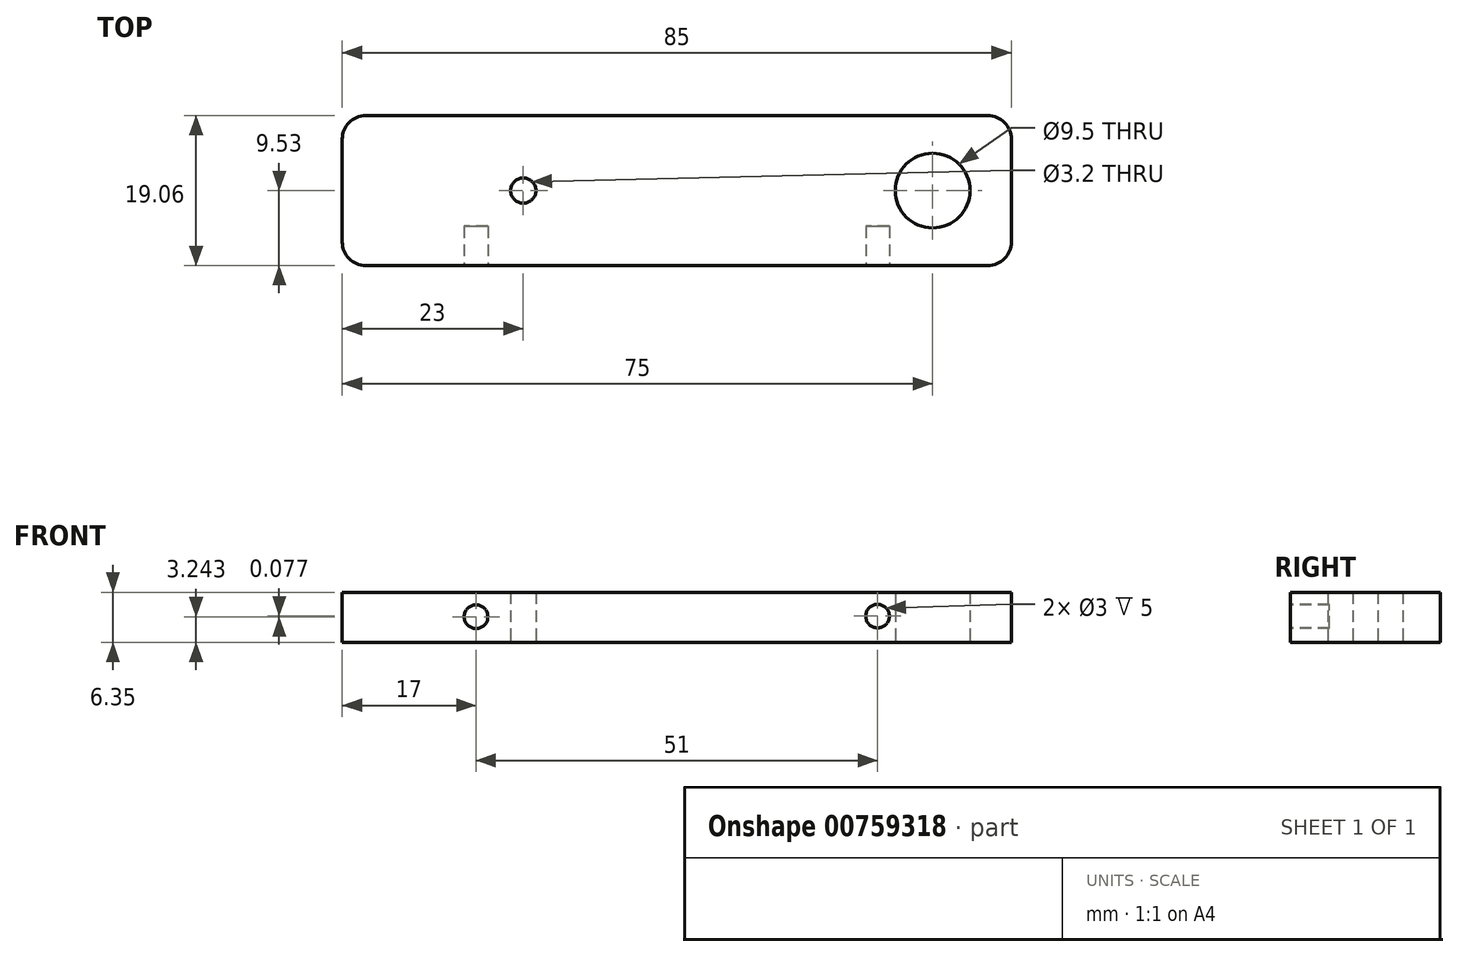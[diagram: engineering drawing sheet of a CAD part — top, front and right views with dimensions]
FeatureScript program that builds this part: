
annotation { "Feature Type Name" : "Feature", "Feature Type Description" : "" }
export const myFeature = defineFeature(function(context is Context, id is Id, definition is map)
    precondition{}
    {
        {
            var Q0;
            Q0=qCreatedBy(makeId("Top.planeOp"),FACE);
            var sketch = newSketch(context, id + "F0", { "sketchPlane" : qUnion([Q0])});
            skLineSegment(sketch, "E0.bottom", {"start": v(-42.5, 9.52) * mm, "end": v(42.5, 9.52) * mm});
            skLineSegment(sketch, "E0.top", {"start": v(-42.5, -9.52) * mm, "end": v(42.5, -9.52) * mm});
            skLineSegment(sketch, "E0.left", {"start": v(-42.5, 9.52) * mm, "end": v(-42.5, -9.52) * mm});
            skLineSegment(sketch, "E0.right", {"start": v(42.5, 9.52) * mm, "end": v(42.5, -9.52) * mm});
            skPoint(sketch, "E0.middle", {"position": v(0, 0) * mm});
            skCircle(sketch, "E1", {"center": v(32.5, 0) * mm, "radius": 4.75 * mm});
            skCircle(sketch, "E2", {"center": v(-19.5, 0) * mm, "radius": 1.6 * mm});
            skSolve(sketch);
        }
        {
            var Q0;
            Q0=makeQuery(id+"F0.imprint","IMPRINT",FACE,{"disambiguationData":[TD([[makeQuery(id+"F0.imprint","IMPRINT",EDGE,{"derivedFrom":sQuery(id+"F0.wireOp",EDGE,"E0.bottom")}),-1.0]])]});
            extrude(context, id + "F1", {"entities" : qUnion([Q0]), "depth" : 6.35 * mm, "offsetDistance" : 25 * mm});
        }
        {
            var Q0;
            Q0=makeQuery(id+"F1.opExtrude","SWEPT_FACE",FACE,{"disambiguationData":[OSD([sQuery(id+"F0.wireOp",EDGE,"E0.top")])]});
            var sketch = newSketch(context, id + "F2", { "sketchPlane" : qUnion([Q0])});
            skCircle(sketch, "E3", {"center": v(-25.5, 3.24) * mm, "radius": 1.5 * mm});
            skCircle(sketch, "E4", {"center": v(25.5, 3.32) * mm, "radius": 1.5 * mm});
            skSolve(sketch);
        }
        {
            var Q0;
            Q0=makeQuery(id+"F2.imprint","IMPRINT",FACE,{"disambiguationData":[TD([[makeQuery(id+"F2.imprint","IMPRINT",EDGE,{"derivedFrom":sQuery(id+"F2.wireOp",EDGE,"E3")}),1.0]])]});
            var Q1;
            Q1=makeQuery(id+"F2.imprint","IMPRINT",FACE,{"disambiguationData":[TD([[makeQuery(id+"F2.imprint","IMPRINT",EDGE,{"derivedFrom":sQuery(id+"F2.wireOp",EDGE,"E4")}),1.0]])]});
            extrude(context, id + "F3", {"entities" : qUnion([Q0, Q1]), "operationType" : NewBodyOperationType.REMOVE, "oppositeDirection" : true, "depth" : 5 * mm, "offsetDistance" : 25 * mm});
        }
        {
            var Q0;
            Q0=makeQuery(id+"F1.opExtrude","SWEPT_EDGE",EDGE,{"disambiguationData":[OSD([sQuery(id+"F0.wireOp",EDGE,"E0.bottom"),sQuery(id+"F0.wireOp",EDGE,"E0.left")])]});
            var Q1;
            Q1=makeQuery(id+"F1.opExtrude","SWEPT_EDGE",EDGE,{"disambiguationData":[OSD([sQuery(id+"F0.wireOp",EDGE,"E0.top"),sQuery(id+"F0.wireOp",EDGE,"E0.left")])]});
            var Q2;
            Q2=makeQuery(id+"F1.opExtrude","SWEPT_EDGE",EDGE,{"disambiguationData":[OSD([sQuery(id+"F0.wireOp",EDGE,"E0.bottom"),sQuery(id+"F0.wireOp",EDGE,"E0.right")])]});
            var Q3;
            Q3=makeQuery(id+"F1.opExtrude","SWEPT_EDGE",EDGE,{"disambiguationData":[OSD([sQuery(id+"F0.wireOp",EDGE,"E0.top"),sQuery(id+"F0.wireOp",EDGE,"E0.right")])]});
            fillet(context, id + "F4", {"entities" : qUnion([Q0, Q1, Q2, Q3]), "radius" : 3 * mm, "tangentPropagation" : true, "allowEdgeOverflow" : false});
        }
    });
